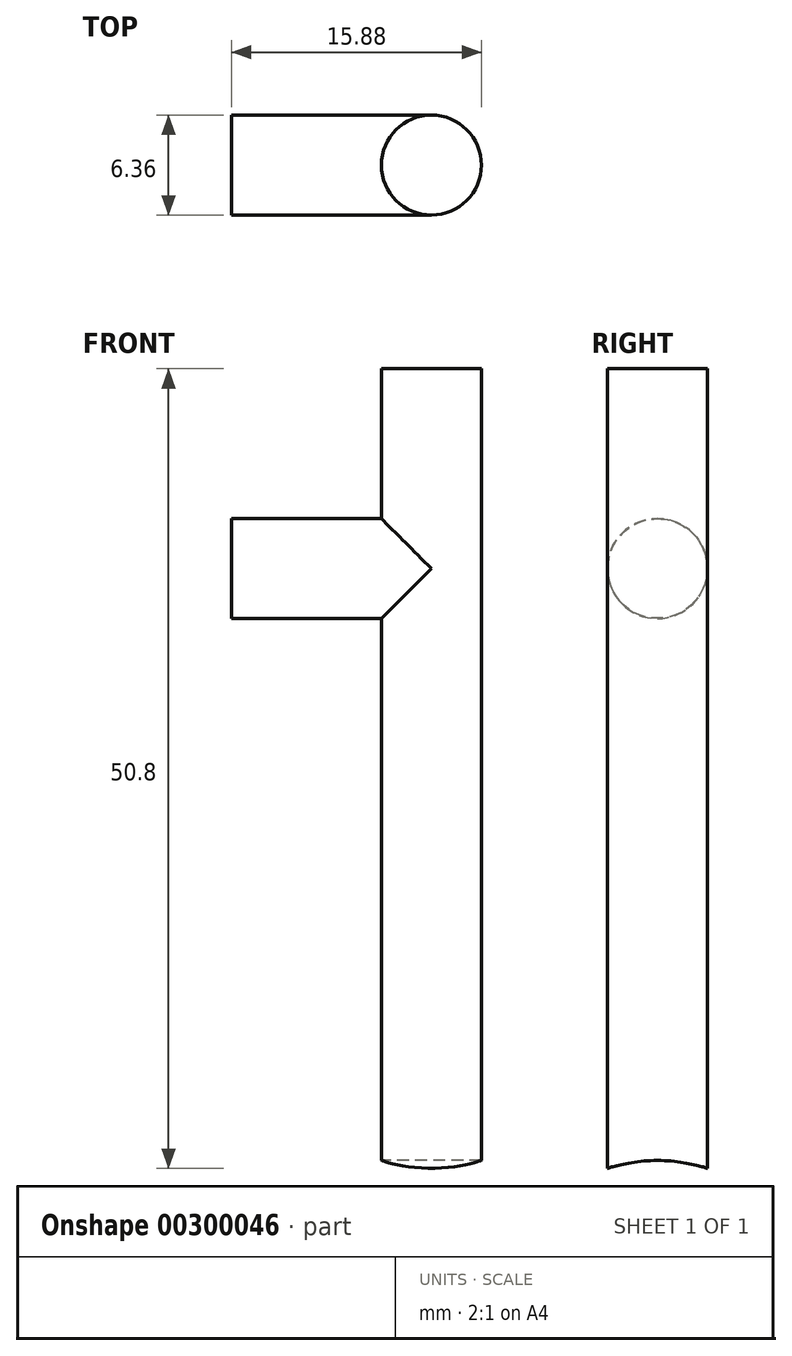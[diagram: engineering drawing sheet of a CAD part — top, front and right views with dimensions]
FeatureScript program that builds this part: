
annotation { "Feature Type Name" : "Feature", "Feature Type Description" : "" }
export const myFeature = defineFeature(function(context is Context, id is Id, definition is map)
    precondition{}
    {
        {
            var Q0;
            Q0=qCreatedBy(makeId("Top.planeOp"),FACE);
            var sketch = newSketch(context, id + "F0", { "sketchPlane" : qUnion([Q0])});
            skLineSegment(sketch, "E0.bottom", {"start": v(6.35, 0) * mm, "end": v(-6.35, 0) * mm});
            skLineSegment(sketch, "E0.top", {"start": v(6.35, -3.18) * mm, "end": v(-6.35, -3.17) * mm});
            skLineSegment(sketch, "E0.left", {"start": v(6.35, 0) * mm, "end": v(6.35, -3.18) * mm});
            skLineSegment(sketch, "E0.right", {"start": v(-6.35, 0) * mm, "end": v(-6.35, -3.17) * mm});
            skPoint(sketch, "E0.middle", {"position": v(0, -1.59) * mm});
            skLineSegment(sketch, "E1", {"start": v(-16.8, 0) * mm, "end": v(21.3, 0) * mm, "construction": true});
            skSolve(sketch);
        }
        {
            var Q0;
            Q0 = qSketchRegion(id + "F0", true);
            var Q1;
            Q1=sQuery(id+"F0.wireOp",EDGE,"E1");
            revolve(context, id + "F1", {"entities" : qUnion([Q0]), "axis" : qUnion([Q1]), "revolveType" : RevolveType.FULL});
        }
        {
            var Q0;
            Q0=qCreatedBy(makeId("Top.planeOp"),FACE);
            var sketch = newSketch(context, id + "F2", { "sketchPlane" : qUnion([Q0])});
            skCircle(sketch, "E2", {"center": v(6.35, 0) * mm, "radius": 3.18 * mm});
            skSolve(sketch);
        }
        {
            var Q0;
            Q0 = qSketchRegion(id + "F2", true);
            extrude(context, id + "F3", {"entities" : qUnion([Q0]), "operationType" : NewBodyOperationType.REMOVE, "endBound" : BoundingType.SYMMETRIC, "oppositeDirection" : true, "depth" : 6.35 * mm});
        }
        {
            var Q0;
            Q0=qCreatedBy(makeId("Top.planeOp"),FACE);
            cPlane(context, id + "F4", {"entities" : qUnion([Q0]), "cplaneType" : CPlaneType.OFFSET, "offset" : 12.7 * mm, "width" : 152.4 * mm, "height" : 152.4 * mm});
        }
        {
            var Q0;
            Q0=qCreatedBy(id+"F4.planeOp",FACE);
            var sketch = newSketch(context, id + "F5", { "sketchPlane" : qUnion([Q0])});
            skCircle(sketch, "E3", {"center": v(6.35, 0) * mm, "radius": 3.18 * mm});
            skSolve(sketch);
        }
        {
            var Q0;
            Q0 = qSketchRegion(id + "F5", true);
            extrude(context, id + "F6", {"entities" : qUnion([Q0]), "operationType" : NewBodyOperationType.ADD, "oppositeDirection" : true, "depth" : 50.8 * mm});
        }
        {
            var Q0;
            Q0=qCreatedBy(makeId("Right.planeOp"),FACE);
            var sketch = newSketch(context, id + "F7", { "sketchPlane" : qUnion([Q0])});
            skCircle(sketch, "E4", {"center": v(0, -47.75) * mm, "radius": 10.16 * mm});
            skLineSegment(sketch, "E5", {"start": v(3.18, 0) * mm, "end": v(3.18, -38.1) * mm, "construction": true});
            skLineSegment(sketch, "E6", {"start": v(-3.18, 0) * mm, "end": v(-3.17, -38.1) * mm, "construction": true});
            skSolve(sketch);
        }
        {
            var Q0;
            Q0 = qSketchRegion(id + "F7", true);
            extrude(context, id + "F8", {"entities" : qUnion([Q0]), "operationType" : NewBodyOperationType.REMOVE, "depth" : 25.4 * mm});
        }
    });
